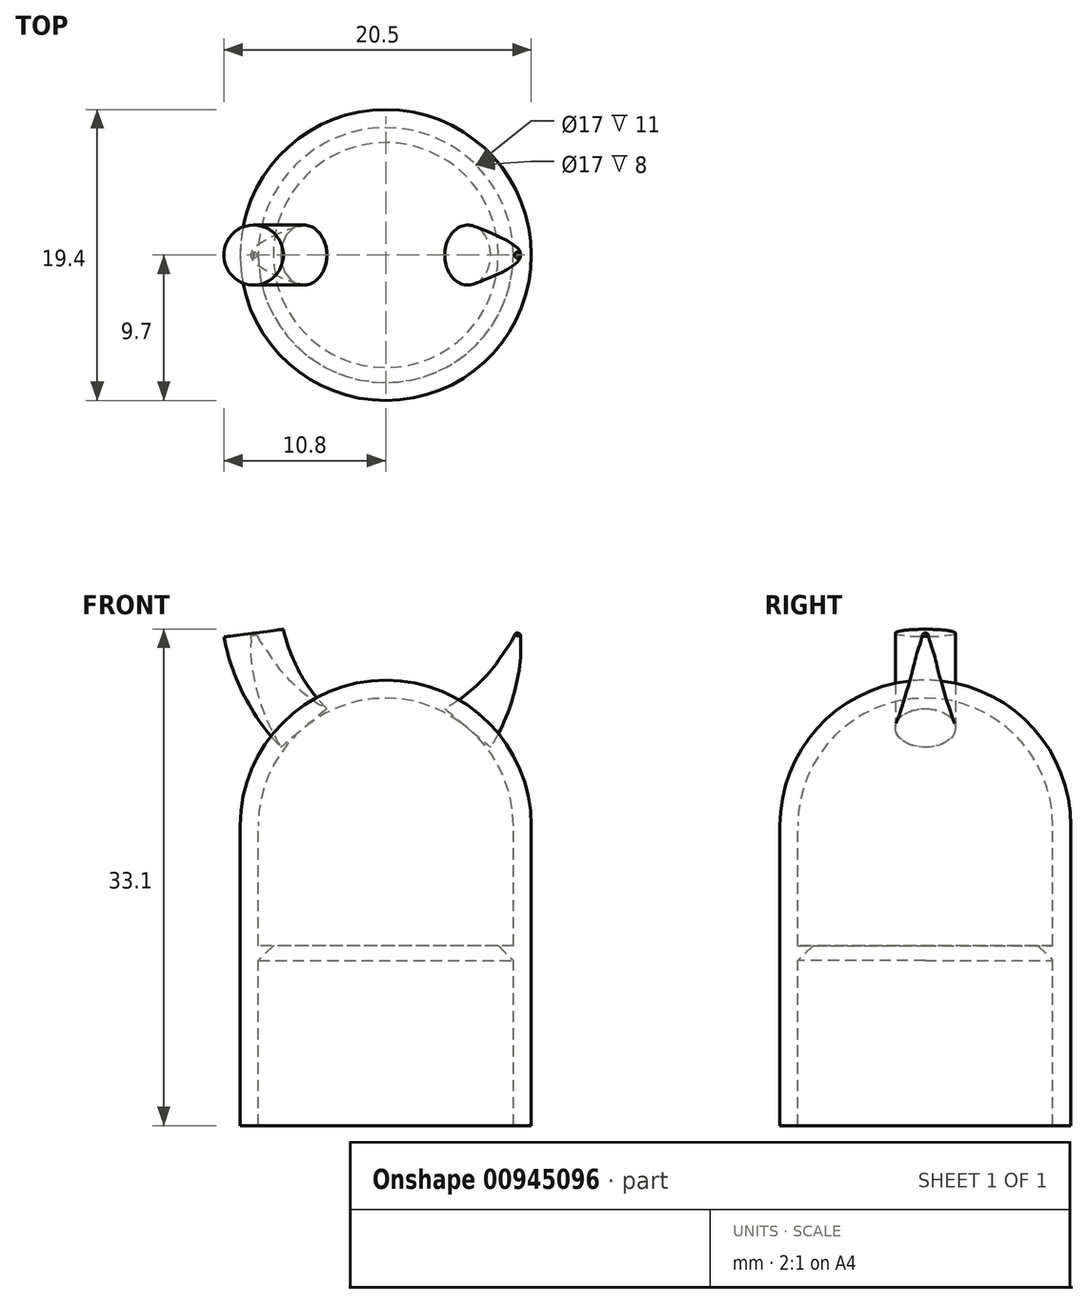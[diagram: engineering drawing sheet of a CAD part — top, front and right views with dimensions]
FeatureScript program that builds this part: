
annotation { "Feature Type Name" : "Feature", "Feature Type Description" : "" }
export const myFeature = defineFeature(function(context is Context, id is Id, definition is map)
    precondition{}
    {
        {
            var Q0;
            Q0=qCreatedBy(makeId("Top.planeOp"),FACE);
            var sketch = newSketch(context, id + "F0", { "sketchPlane" : qUnion([Q0])});
            skCircle(sketch, "E0", {"center": v(0, 0) * mm, "radius": 8.5 * mm});
            skCircle(sketch, "E1", {"center": v(0, 0) * mm, "radius": 9.7 * mm});
            skLineSegment(sketch, "E2", {"start": v(0, 0) * mm, "end": v(-18.37, 0) * mm, "construction": true});
            skLineSegment(sketch, "E3", {"start": v(8.5, 0) * mm, "end": v(9.7, 0) * mm});
            skLineSegment(sketch, "E4", {"start": v(-9.7, 0) * mm, "end": v(-8.5, 0) * mm});
            skCircle(sketch, "E5", {"center": v(0, 0) * mm, "radius": 7.5 * mm});
            skSolve(sketch);
        }
        {
            var Q0;
            {var subQ0=sQuery(id+"F0.wireOp",EDGE,"E3");Q0=makeQuery(id+"F0.imprint","IMPRINT",FACE,{"disambiguationData":[TD([[makeQuery(id+"F0.imprint","IMPRINT",EDGE,{"derivedFrom":subQ0}),-1.0]])]});}
            var Q1;
            {var subQ0=sQuery(id+"F0.wireOp",EDGE,"E3");Q1=makeQuery(id+"F0.imprint","IMPRINT",FACE,{"disambiguationData":[TD([[makeQuery(id+"F0.imprint","IMPRINT",EDGE,{"derivedFrom":subQ0}),1.0]])]});}
            extrude(context, id + "F1", {"entities" : qUnion([Q0, Q1]), "oppositeDirection" : true, "depth" : 20 * mm, "offsetDistance" : 25 * mm});
        }
        {
            var Q0;
            Q0=makeQuery(id+"F0.imprint","IMPRINT",FACE,{"disambiguationData":[TD([[makeQuery(id+"F0.imprint","IMPRINT",EDGE,{"derivedFrom":sQuery(id+"F0.wireOp",EDGE,"E5")}),-1.0]])]});
            extrude(context, id + "F2", {"entities" : qUnion([Q0]), "operationType" : NewBodyOperationType.ADD, "oppositeDirection" : true, "depth" : 10 * mm, "offsetDistance" : 25 * mm, "hasSecondDirection" : true, "secondDirectionOppositeDirection" : true, "secondDirectionDepth" : 8 * mm});
        }
        {
            var Q0;
            Q0=makeQuery(id+"F2.opExtrude","CAP_EDGE",EDGE,{"disambiguationData":[OSD([sQuery(id+"F0.wireOp",EDGE,"E5")])],"isStart":false});
            chamfer(context, id + "F3", {"entities" : qUnion([Q0]), "width" : 2 * mm, "tangentPropagation" : true});
        }
        {
            var Q0;
            {var subQ0=sQuery(id+"F0.wireOp",EDGE,"E3");Q0=makeQuery(id+"F0.imprint","IMPRINT",FACE,{"disambiguationData":[TD([[makeQuery(id+"F0.imprint","IMPRINT",EDGE,{"derivedFrom":subQ0}),1.0]])]});}
            var Q1;
            Q1=sQuery(id+"F0.wireOp",EDGE,"E2");
            revolve(context, id + "F4", {"operationType" : NewBodyOperationType.ADD, "surfaceOperationType" : NewSurfaceOperationType.NEW, "entities" : qUnion([Q0]), "axis" : qUnion([Q1]), "revolveType" : RevolveType.ONE_DIRECTION, "oppositeDirection" : true, "angle" : 180 * degree});
        }
        {
            var Q0;
            Q0=qCreatedBy(makeId("Front.planeOp"),FACE);
            var sketch = newSketch(context, id + "F5", { "sketchPlane" : qUnion([Q0])});
            skLineSegment(sketch, "E6", {"start": v(0, 0) * mm, "end": v(-5.46, 6.51) * mm, "construction": true});
            skLineSegment(sketch, "E7", {"start": v(0, 0) * mm, "end": v(0, 11.53) * mm, "construction": true});
            skLineSegment(sketch, "E8", {"start": v(-5.46, 6.51) * mm, "end": v(-8.68, 10.34) * mm, "construction": true});
            skLineSegment(sketch, "E9", {"start": v(-5.46, 6.51) * mm, "end": v(-4.31, 7.48) * mm});
            skArc(sketch, "E10", {"start": v(-8.81, 12.84) * mm, "mid": v(-7.6, 9.43) * mm, "end": v(-5.46, 6.51) * mm});
            skLineSegment(sketch, "E11", {"start": v(-8.81, 12.84) * mm, "end": v(-4.31, 7.48) * mm, "construction": true});
            skSolve(sketch);
        }
        {
            var Q0;
            Q0=sQuery(id+"F5.wireOp",EDGE,"E9");
            cPlane(context, id + "F6", {"entities" : qUnion([Q0]), "cplaneType" : CPlaneType.LINE_ANGLE, "offset" : 25 * mm, "angle" : 90 * degree, "width" : 150 * mm, "height" : 150 * mm});
        }
        {
            var Q0;
            Q0=qCreatedBy(id+"F6.planeOp",FACE);
            var sketch = newSketch(context, id + "F7", { "sketchPlane" : qUnion([Q0])});
            skCircle(sketch, "E12", {"center": v(0, 0) * mm, "radius": 2 * mm});
            skSolve(sketch);
        }
        {
            var Q0;
            Q0=makeQuery(id+"F7.imprint","IMPRINT",FACE,{"disambiguationData":[TD([[makeQuery(id+"F7.imprint","IMPRINT",EDGE,{"derivedFrom":sQuery(id+"F7.wireOp",EDGE,"E12")}),1.0]])]});
            var Q1;
            Q1=sQuery(id+"F5.wireOp",EDGE,"E10");
            sweep(context, id + "F8", {"profiles" : qUnion([Q0]), "path" : qUnion([Q1])});
        }
        {
            var Q0;
            Q0=makeQuery(id+"F8.opSweep","CAP_FACE",FACE,{"disambiguationData":[OSD([sQuery(id+"F5.wireOp",VERTEX,"E10.start"),sQuery(id+"F7.wireOp",EDGE,"E12")])],"isStart":false});
            var sketch = newSketch(context, id + "F9", { "sketchPlane" : qUnion([Q0])});
            skCircle(sketch, "E13", {"center": v(-7.08, 0) * mm, "radius": 0.2 * mm});
            skSolve(sketch);
        }
        {
            var Q0;
            Q0=sQuery(id+"F5.wireOp",EDGE,"E10");
            var Q1;
            Q1=makeQuery(id+"F9.imprint","IMPRINT",FACE,{"disambiguationData":[TD([[makeQuery(id+"F9.imprint","IMPRINT",EDGE,{"derivedFrom":sQuery(id+"F9.wireOp",EDGE,"E13")}),1.0]])]});
            var Q2;
            Q2=makeQuery(id+"F8.opSweep","CAP_FACE",FACE,{"disambiguationData":[OSD([sQuery(id+"F5.wireOp",VERTEX,"E10.end"),sQuery(id+"F7.wireOp",EDGE,"E12")])],"isStart":true});
            loft(context, id + "F10", {"addSections" : true, "spine" : qUnion([Q0]), "sectionCount" : 5, "startCondition" : LoftEndDerivativeType.NORMAL_TO_PROFILE, "startMagnitude" : 1, "sheetProfilesArray" : [{ "sheetProfileEntities" : qUnion([Q1]) }, { "sheetProfileEntities" : qUnion([Q2]) }]});
        }
        {
            var Q0;
            Q0=makeQuery(id+"F10.opLoft","CAP_FACE",FACE,{"disambiguationData":[OSD([makeQuery(id+"F9.imprint","IMPRINT",FACE,{"disambiguationData":[TD([[makeQuery(id+"F9.imprint","IMPRINT",EDGE,{"derivedFrom":sQuery(id+"F9.wireOp",EDGE,"E13")}),1.0]])]})])],"isStart":true});
            fillet(context, id + "F11", {"entities" : qUnion([Q0]), "radius" : .2 * mm, "tangentPropagation" : true, "allowEdgeOverflow" : false});
        }
        {
            var Q0;
            Q0=makeQuery(id+"F10.opLoft","SWEPT_BODY",BODY,{"disambiguationData":[OSD([sQuery(id+"F5.wireOp",VERTEX,"E10.end"),sQuery(id+"F7.wireOp",EDGE,"E12"),makeQuery(id+"F9.imprint","IMPRINT",FACE,{"disambiguationData":[TD([[makeQuery(id+"F9.imprint","IMPRINT",EDGE,{"derivedFrom":sQuery(id+"F9.wireOp",EDGE,"E13")}),1.0]])]})])]});
            var Q1;
            Q1=sQuery(id+"F5.wireOp",EDGE,"E7");
            transform(context, id + "F12", {"entities" : qUnion([Q0]), "transformType" : TransformType.ROTATION, "transformAxis" : qUnion([Q1]), "angle" : 180 * degree, "makeCopy" : true});
        }
    });
